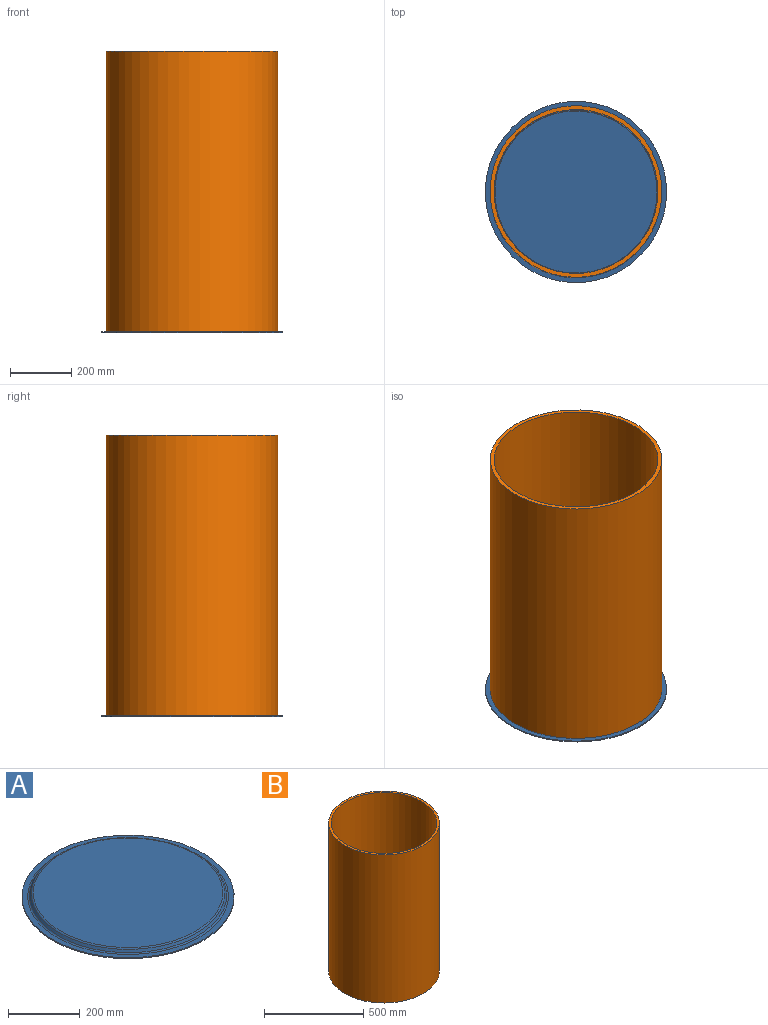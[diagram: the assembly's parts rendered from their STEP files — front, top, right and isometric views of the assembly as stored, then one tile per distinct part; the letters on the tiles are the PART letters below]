
ASSEMBLY  parts=2 mates=1
PART A: 10 faces, bbox 619.6x619.6x16.1 mm
  f0: cone r=271.27mm half-angle=35.1deg, axis (0,0,-1), area 17597.9mm2, adj f1,f9
  f1: torus R=279.27mm, axis (0,0,1), area 16189.1mm2, adj f0,f2
  f2: plane 590.04x590.04mm, normal (0,0,-1), area 28417.4mm2, adj f1,f3
  f3: cylinder r=295.02mm len=590.04mm, axis (0,0,1), area 6356.2mm2, adj f2,f4
  f4: plane 590.04x590.04mm, normal (0,0,1), area 28417.4mm2, adj f3,f5
  f5: torus R=279.27mm, axis (0,0,1), area 10570.6mm2, adj f4,f6
  f6: cone r=274.07mm half-angle=35.1deg, axis (0,0,-1), area 15221.5mm2, adj f5,f7
  f7: torus R=263.75mm, axis (0,0,1), area 10192.5mm2, adj f6,f8
  f8: plane 527.5x527.5mm, normal (0,0,1), area 218540.5mm2, adj f7
  f9: plane 530.53x530.53mm, normal (0,0,-1), area 221062.8mm2, adj f0
PART B: 4 faces, bbox 558.8x558.8x914.4 mm
  f0: cylinder r=266.7mm len=914.4mm, axis (0,0,-1), area 1532283.4mm2, adj f2,f3
  f1: cylinder r=279.4mm len=914.4mm, axis (0,0,-1), area 1605249.3mm2, adj f2,f3
  f2: plane 558.8x558.8mm, normal (0,0,1), area 21788.4mm2, adj f0,f1
  f3: plane 558.8x558.8mm, normal (0,0,-1), area 21788.4mm2, adj f0,f1
PLACE A t=(0,0,3.43)mm
PLACE B t=(0,0,-9.27)mm
MATE fastened B.f0 <-> A.f0  axis (0,0,-1) through (0,0,-9.27)mm
